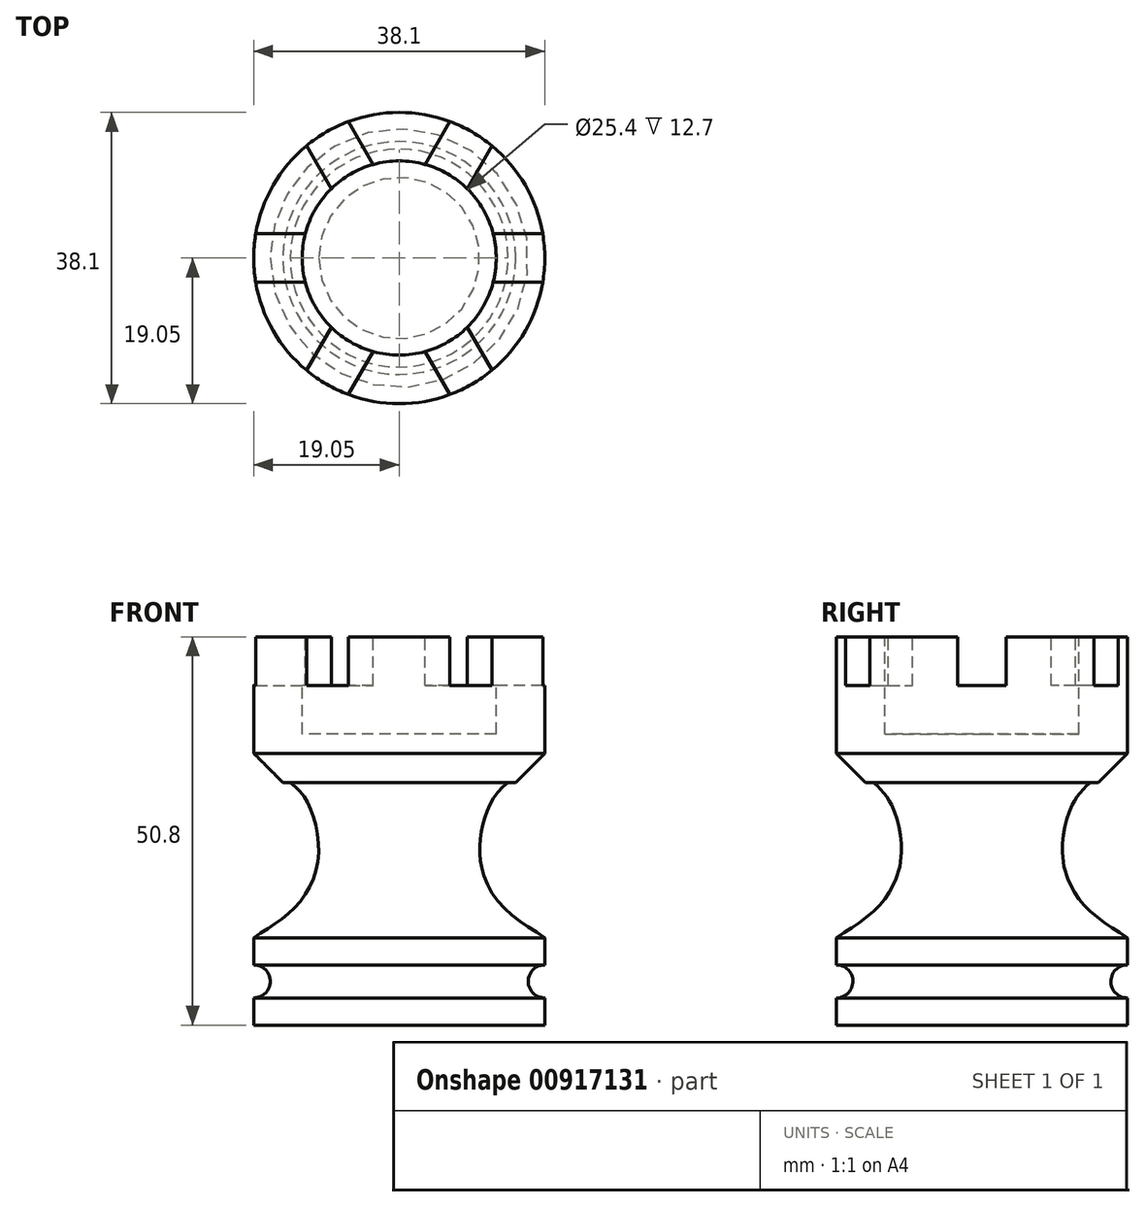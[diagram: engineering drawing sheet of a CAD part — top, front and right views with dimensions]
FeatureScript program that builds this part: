
annotation { "Feature Type Name" : "Feature", "Feature Type Description" : "" }
export const myFeature = defineFeature(function(context is Context, id is Id, definition is map)
    precondition{}
    {
        {
            var Q0;
            Q0=qCreatedBy(makeId("Front.planeOp"),FACE);
            var sketch = newSketch(context, id + "F0", { "sketchPlane" : qUnion([Q0])});
            skLineSegment(sketch, "E0", {"start": v(0, 0) * mm, "end": v(0, 50.8) * mm});
            skLineSegment(sketch, "E1", {"start": v(0, 0) * mm, "end": v(19.05, 0) * mm});
            skLineSegment(sketch, "E2", {"start": v(19.05, 0) * mm, "end": v(19.05, 11.43) * mm});
            skLineSegment(sketch, "E3", {"start": v(0, 31.75) * mm, "end": v(45.34, 31.75) * mm, "construction": true});
            skLineSegment(sketch, "E4.bottom", {"start": v(0, 31.75) * mm, "end": v(19.05, 31.75) * mm});
            skLineSegment(sketch, "E4.top", {"start": v(0, 34.92) * mm, "end": v(19.05, 34.92) * mm});
            skLineSegment(sketch, "E4.left", {"start": v(0, 31.75) * mm, "end": v(0, 34.92) * mm});
            skLineSegment(sketch, "E4.right", {"start": v(19.05, 31.75) * mm, "end": v(19.05, 34.92) * mm});
            skFitSpline(sketch, "E5", {"points": [v(19.05, 11.43) * mm, v(13.73, 15.32) * mm, v(10.64, 21.45) * mm, v(11.68, 28.43) * mm, v(14.25, 31.75) * mm], "startDerivative": vector(-20.72, 13.95) * mm, "endDerivative": vector(16.66, 12.87) * mm});
            skLineSegment(sketch, "E6.top", {"start": v(0, 50.8) * mm, "end": v(19.05, 50.8) * mm});
            skLineSegment(sketch, "E6.left", {"start": v(0, 34.92) * mm, "end": v(0, 50.8) * mm});
            skLineSegment(sketch, "E6.right", {"start": v(19.05, 34.92) * mm, "end": v(19.05, 50.8) * mm});
            skSolve(sketch);
        }
        {
            var Q0;
            {var subQ0=sQuery(id+"F0.wireOp",EDGE,"E4.top");Q0=makeQuery(id+"F0.imprint","IMPRINT",FACE,{"disambiguationData":[TD([[makeQuery(id+"F0.imprint","IMPRINT",EDGE,{"derivedFrom":subQ0}),1.0]])]});}
            var Q1;
            {var subQ5=sQuery(id+"F0.wireOp",EDGE,"E4.top");Q1=makeQuery(id+"F0.imprint","IMPRINT",FACE,{"disambiguationData":[TD([[makeQuery(id+"F0.imprint","IMPRINT",EDGE,{"derivedFrom":subQ5}),-1.0]])]});}
            var Q2;
            {var subQ0=sQuery(id+"F0.wireOp",EDGE,"E1");Q2=makeQuery(id+"F0.imprint","IMPRINT",FACE,{"disambiguationData":[TD([[makeQuery(id+"F0.imprint","IMPRINT",EDGE,{"derivedFrom":subQ0}),1.0]])]});}
            var Q3;
            Q3=sQuery(id+"F0.wireOp",EDGE,"E6.left");
            revolve(context, id + "F1", {"surfaceOperationType" : NewSurfaceOperationType.NEW, "entities" : qUnion([Q0, Q1, Q2]), "axis" : qUnion([Q3]), "revolveType" : RevolveType.FULL});
        }
        {
            var Q0;
            Q0=makeQuery(id+"F1.opRevolve","SWEPT_FACE",FACE,{"disambiguationData":[OSD([sQuery(id+"F0.wireOp",EDGE,"E6.top")])]});
            var sketch = newSketch(context, id + "F2", { "sketchPlane" : qUnion([Q0])});
            skCircle(sketch, "E7", {"center": v(0, 0) * mm, "radius": 12.7 * mm});
            skSolve(sketch);
        }
        {
            var Q0;
            Q0=makeQuery(id+"F2.imprint","IMPRINT",FACE,{"disambiguationData":[TD([[makeQuery(id+"F2.imprint","IMPRINT",EDGE,{"derivedFrom":sQuery(id+"F2.wireOp",EDGE,"E7")}),1.0]])]});
            extrude(context, id + "F3", {"entities" : qUnion([Q0]), "operationType" : NewBodyOperationType.REMOVE, "oppositeDirection" : true, "depth" : 12.7 * mm, "offsetDistance" : 25.4 * mm});
        }
        {
            var Q0;
            Q0=makeQuery(id+"F1.opRevolve","SWEPT_FACE",FACE,{"disambiguationData":[OSD([sQuery(id+"F0.wireOp",EDGE,"E6.top")])]});
            var sketch = newSketch(context, id + "F4", { "sketchPlane" : qUnion([Q0])});
            skLineSegment(sketch, "E8", {"start": v(0, 0) * mm, "end": v(25.6, 0) * mm, "construction": true});
            skLineSegment(sketch, "E9.bottom", {"start": v(25.6, -3.18) * mm, "end": v(7.16, -3.18) * mm});
            skLineSegment(sketch, "E9.top", {"start": v(25.6, 3.17) * mm, "end": v(7.16, 3.17) * mm});
            skLineSegment(sketch, "E9.left", {"start": v(25.6, -3.18) * mm, "end": v(25.6, 3.17) * mm});
            skLineSegment(sketch, "E9.right", {"start": v(7.16, -3.18) * mm, "end": v(7.16, 3.17) * mm});
            skPoint(sketch, "E9.middle", {"position": v(16.38, 0) * mm});
            skLineSegment(sketch, "E10.1.0", {"start": v(15.55, 20.59) * mm, "end": v(10.05, 23.76) * mm});
            skLineSegment(sketch, "E10.1.1", {"start": v(10.05, 23.76) * mm, "end": v(0.83, 7.79) * mm});
            skLineSegment(sketch, "E10.1.2", {"start": v(6.33, 4.61) * mm, "end": v(0.83, 7.79) * mm});
            skLineSegment(sketch, "E10.1.3", {"start": v(15.55, 20.59) * mm, "end": v(6.33, 4.61) * mm});
            skPoint(sketch, "E10.1.4", {"position": v(8.2, 14.19) * mm});
            skLineSegment(sketch, "E10.2.0", {"start": v(-10.05, 23.76) * mm, "end": v(-15.55, 20.59) * mm});
            skLineSegment(sketch, "E10.2.1", {"start": v(-15.55, 20.59) * mm, "end": v(-6.33, 4.61) * mm});
            skLineSegment(sketch, "E10.2.2", {"start": v(-0.83, 7.79) * mm, "end": v(-6.33, 4.61) * mm});
            skLineSegment(sketch, "E10.2.3", {"start": v(-10.05, 23.76) * mm, "end": v(-0.83, 7.79) * mm});
            skPoint(sketch, "E10.2.4", {"position": v(-8.2, 14.19) * mm});
            skLineSegment(sketch, "E10.3.0", {"start": v(-25.6, 3.18) * mm, "end": v(-25.6, -3.17) * mm});
            skLineSegment(sketch, "E10.3.1", {"start": v(-25.6, -3.17) * mm, "end": v(-7.16, -3.17) * mm});
            skLineSegment(sketch, "E10.3.2", {"start": v(-7.16, 3.18) * mm, "end": v(-7.16, -3.17) * mm});
            skLineSegment(sketch, "E10.3.3", {"start": v(-25.6, 3.18) * mm, "end": v(-7.16, 3.18) * mm});
            skPoint(sketch, "E10.3.4", {"position": v(-16.38, 0) * mm});
            skLineSegment(sketch, "E10.4.0", {"start": v(-15.55, -20.59) * mm, "end": v(-10.05, -23.76) * mm});
            skLineSegment(sketch, "E10.4.1", {"start": v(-10.05, -23.76) * mm, "end": v(-0.83, -7.79) * mm});
            skLineSegment(sketch, "E10.4.2", {"start": v(-6.33, -4.61) * mm, "end": v(-0.83, -7.79) * mm});
            skLineSegment(sketch, "E10.4.3", {"start": v(-15.55, -20.59) * mm, "end": v(-6.33, -4.61) * mm});
            skPoint(sketch, "E10.4.4", {"position": v(-8.2, -14.19) * mm});
            skLineSegment(sketch, "E10.5.0", {"start": v(10.05, -23.76) * mm, "end": v(15.55, -20.59) * mm});
            skLineSegment(sketch, "E10.5.1", {"start": v(15.55, -20.59) * mm, "end": v(6.33, -4.61) * mm});
            skLineSegment(sketch, "E10.5.2", {"start": v(0.83, -7.79) * mm, "end": v(6.33, -4.61) * mm});
            skLineSegment(sketch, "E10.5.3", {"start": v(10.05, -23.76) * mm, "end": v(0.83, -7.79) * mm});
            skPoint(sketch, "E10.5.4", {"position": v(8.2, -14.19) * mm});
            skPoint(sketch, "E10.center", {"position": v(0, 0) * mm});
            skSolve(sketch);
        }
        {
            var Q0;
            Q0=qSketchRegion(id+"F4",true);
            extrude(context, id + "F5", {"entities" : qUnion([Q0]), "operationType" : NewBodyOperationType.REMOVE, "oppositeDirection" : true, "depth" : 6.35 * mm, "offsetDistance" : 25.4 * mm});
        }
        {
            var Q0;
            Q0=makeQuery(id+"F1.opRevolve","SWEPT_EDGE",EDGE,{"disambiguationData":[OSD([sQuery(id+"F0.wireOp",EDGE,"E4.bottom"),sQuery(id+"F0.wireOp",EDGE,"E4.right")])]});
            chamfer(context, id + "F6", {"entities" : qUnion([Q0]), "width" : 3.8 * mm, "tangentPropagation" : true});
        }
        {
            var Q0;
            Q0=qCreatedBy(makeId("Front.planeOp"),FACE);
            var sketch = newSketch(context, id + "F7", { "sketchPlane" : qUnion([Q0])});
            skLineSegment(sketch, "E11", {"start": v(0, 5.72) * mm, "end": v(19.05, 5.72) * mm, "construction": true});
            skCircle(sketch, "E12", {"center": v(19.05, 5.72) * mm, "radius": 2.16 * mm});
            skLineSegment(sketch, "E13", {"start": v(19.05, 11.43) * mm, "end": v(19.05, 0) * mm});
            skSolve(sketch);
        }
        {
            var Q0;
            Q0=qSketchRegion(id+"F7",true);
            var Q1;
            Q1=makeQuery(id+"F1.opRevolve","SWEPT_FACE",FACE,{"disambiguationData":[OSD([sQuery(id+"F0.wireOp",EDGE,"E2")])]});
            revolve(context, id + "F8", {"operationType" : NewBodyOperationType.REMOVE, "surfaceOperationType" : NewSurfaceOperationType.NEW, "entities" : qUnion([Q0]), "axis" : qUnion([Q1]), "revolveType" : RevolveType.FULL, "oppositeDirection" : true});
        }
    });
